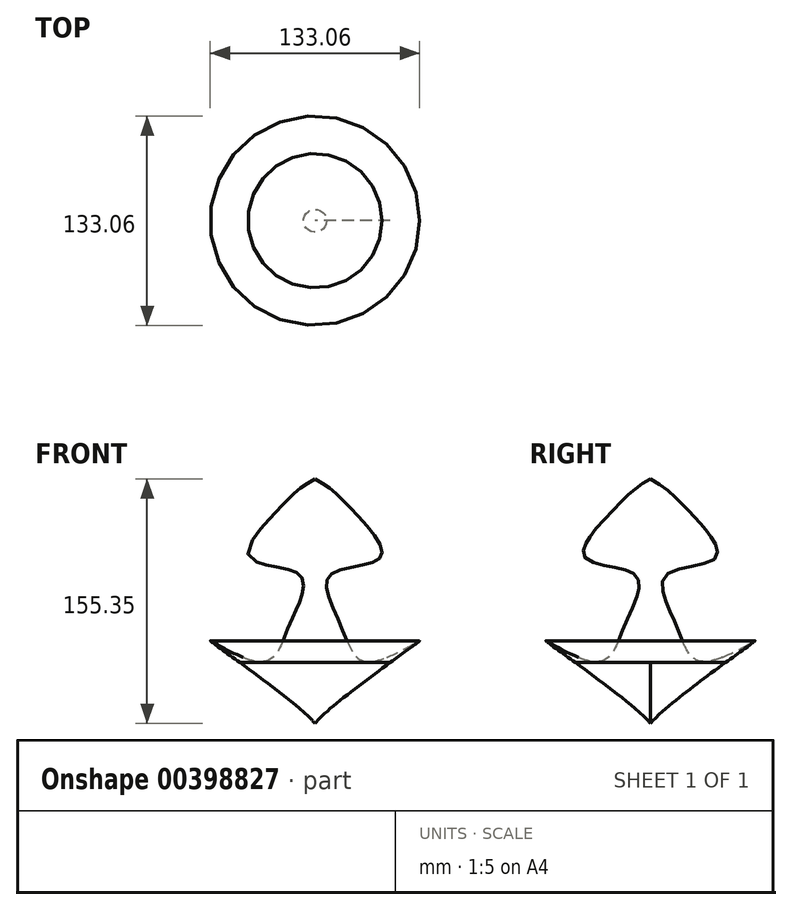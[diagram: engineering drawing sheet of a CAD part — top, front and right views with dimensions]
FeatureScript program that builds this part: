
annotation { "Feature Type Name" : "Feature", "Feature Type Description" : "" }
export const myFeature = defineFeature(function(context is Context, id is Id, definition is map)
    precondition{}
    {
        {
            var Q0;
            Q0=qCreatedBy(makeId("Front.planeOp"),FACE);
            var sketch = newSketch(context, id + "F0", { "sketchPlane" : qUnion([Q0])});
            skLineSegment(sketch, "E0", {"start": v(0, 77.25) * mm, "end": v(0, -78.1) * mm});
            skFitSpline(sketch, "E1", {"points": [v(0, 77.25) * mm, v(22.9, 58.43) * mm, v(41.79, 27.5) * mm, v(9.64, 16.25) * mm, v(16.67, -16.5) * mm, v(34.75, -38.8) * mm, v(66.5, -25.54) * mm, v(0, -78.1) * mm], "startDerivative": vector(208, -107.46) * mm, "endDerivative": vector(-127.36, -170.93) * mm});
            skArc(sketch, "E2", {"start": v(47.7, -39.35) * mm, "mid": v(86.38, -13.34) * mm, "end": v(45.66, -36.03) * mm});
            skSolve(sketch);
        }
        {
            var Q0;
            Q0=makeQuery(id+"F0.imprint","IMPRINT",FACE,{"disambiguationData":[TD([[makeQuery(id+"F0.imprint","IMPRINT",EDGE,{"derivedFrom":sQuery(id+"F0.wireOp",EDGE,"E0")}),1.0]])]});
            var Q1;
            Q1=sQuery(id+"F0.wireOp",EDGE,"E0");
            revolve(context, id + "F1", {"entities" : qUnion([Q0]), "axis" : qUnion([Q1]), "revolveType" : RevolveType.FULL});
        }
    });
